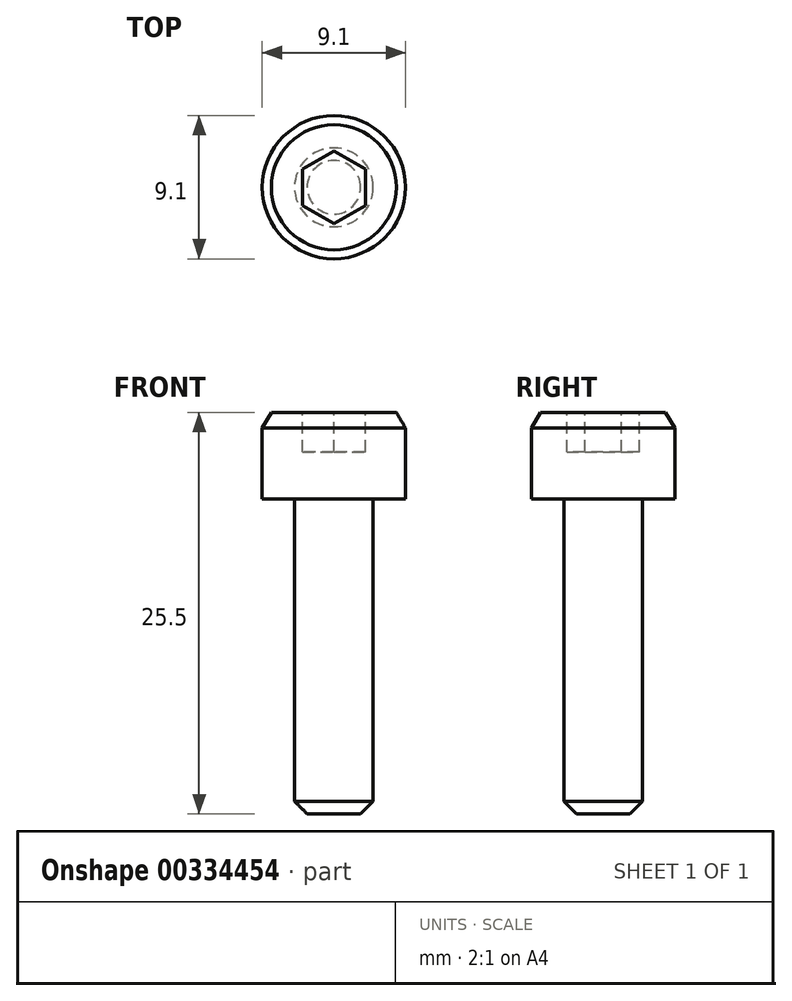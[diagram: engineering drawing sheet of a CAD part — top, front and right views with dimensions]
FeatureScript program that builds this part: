
annotation { "Feature Type Name" : "Feature", "Feature Type Description" : "" }
export const myFeature = defineFeature(function(context is Context, id is Id, definition is map)
    precondition{}
    {
        {
            var Q0;
            Q0=qCreatedBy(makeId("Top.planeOp"),FACE);
            var sketch = newSketch(context, id + "F0", { "sketchPlane" : qUnion([Q0])});
            skCircle(sketch, "E0", {"center": v(0, 0) * mm, "radius": 4.55 * mm});
            skSolve(sketch);
        }
        {
            var Q0;
            Q0=makeQuery(id+"F0.imprint","IMPRINT",FACE,{"disambiguationData":[TD([[makeQuery(id+"F0.imprint","IMPRINT",EDGE,{"derivedFrom":sQuery(id+"F0.wireOp",EDGE,"E0")}),1.0]])]});
            extrude(context, id + "F1", {"entities" : qUnion([Q0]), "oppositeDirection" : true, "depth" : 5.5 * mm});
        }
        {
            var Q0;
            Q0=makeQuery(id+"F1.opExtrude","CAP_FACE",FACE,{"disambiguationData":[OSD([sQuery(id+"F0.wireOp",EDGE,"E0")])],"isStart":false});
            var sketch = newSketch(context, id + "F2", { "sketchPlane" : qUnion([Q0])});
            skCircle(sketch, "E1", {"center": v(0, 0) * mm, "radius": 2.5 * mm});
            skSolve(sketch);
        }
        {
            var Q0;
            Q0=makeQuery(id+"F2.imprint","IMPRINT",FACE,{"disambiguationData":[TD([[makeQuery(id+"F2.imprint","IMPRINT",EDGE,{"derivedFrom":sQuery(id+"F2.wireOp",EDGE,"E1")}),1.0]])]});
            extrude(context, id + "F3", {"entities" : qUnion([Q0]), "operationType" : NewBodyOperationType.ADD, "depth" : 20 * mm});
        }
        {
            var Q0;
            Q0=makeQuery(id+"F1.opExtrude","CAP_FACE",FACE,{"disambiguationData":[OSD([sQuery(id+"F0.wireOp",EDGE,"E0")])],"isStart":true});
            var sketch = newSketch(context, id + "F4", { "sketchPlane" : qUnion([Q0])});
            skCircle(sketch, "E2.cCircle", {"center": v(0, 0) * mm, "radius": 2.3 * mm, "construction": true});
            skLineSegment(sketch, "E2.0", {"start": v(2, -1.16) * mm, "end": v(0, -2.3) * mm});
            skLineSegment(sketch, "E2.1", {"start": v(0, -2.3) * mm, "end": v(-2, -1.15) * mm});
            skLineSegment(sketch, "E2.2", {"start": v(-2, -1.15) * mm, "end": v(-2, 1.16) * mm});
            skLineSegment(sketch, "E2.3", {"start": v(-2, 1.16) * mm, "end": v(0, 2.3) * mm});
            skLineSegment(sketch, "E2.4", {"start": v(0, 2.3) * mm, "end": v(2, 1.15) * mm});
            skLineSegment(sketch, "E2.5", {"start": v(2, 1.15) * mm, "end": v(2, -1.16) * mm});
            skSolve(sketch);
        }
        {
            var Q0;
            Q0=makeQuery(id+"F4.imprint","IMPRINT",FACE,{"disambiguationData":[TD([[makeQuery(id+"F4.imprint","IMPRINT",EDGE,{"derivedFrom":sQuery(id+"F4.wireOp",EDGE,"E2.0")}),-1.0]])]});
            extrude(context, id + "F5", {"entities" : qUnion([Q0]), "operationType" : NewBodyOperationType.REMOVE, "oppositeDirection" : true, "depth" : 2.5 * mm});
        }
        {
            var Q0;
            Q0=makeQuery(id+"F1.opExtrude","CAP_EDGE",EDGE,{"disambiguationData":[OSD([sQuery(id+"F0.wireOp",EDGE,"E0")])],"isStart":true});
            chamfer(context, id + "F6", {"entities" : qUnion([Q0]), "chamferType" : ChamferType.OFFSET_ANGLE, "width" : 1 * mm, "oppositeDirection" : false, "angle" : 30 * degree, "tangentPropagation" : true});
        }
        {
            var Q0;
            Q0=makeQuery(id+"F3.opExtrude","CAP_EDGE",EDGE,{"disambiguationData":[OSD([sQuery(id+"F2.wireOp",EDGE,"E1")])],"isStart":false});
            chamfer(context, id + "F7", {"entities" : qUnion([Q0]), "width" : 0.8 * mm, "tangentPropagation" : true});
        }
    });
